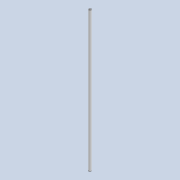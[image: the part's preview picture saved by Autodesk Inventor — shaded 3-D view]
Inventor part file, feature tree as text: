
AUTODESK INVENTOR PART (.ipt)
format: ipt  version: 2020 (Build 240168000, 168)  size: 71,680 bytes
history: native  units: mm
features: extrude x1, sketch x1
ambient origin geometry x8: Origin, YZ Plane, XZ Plane, XY Plane, X Axis, Y Axis, Z Axis, Center Point
bodies: Solid1 (feature_tree)
feature tree (2):
  extrude  "Extrusion1"  Depth=80.0mm
  sketch  "Sketch1"  dims[d0=0.5mm d1=1.4mm d2=80.0mm d3=0.0mm]
